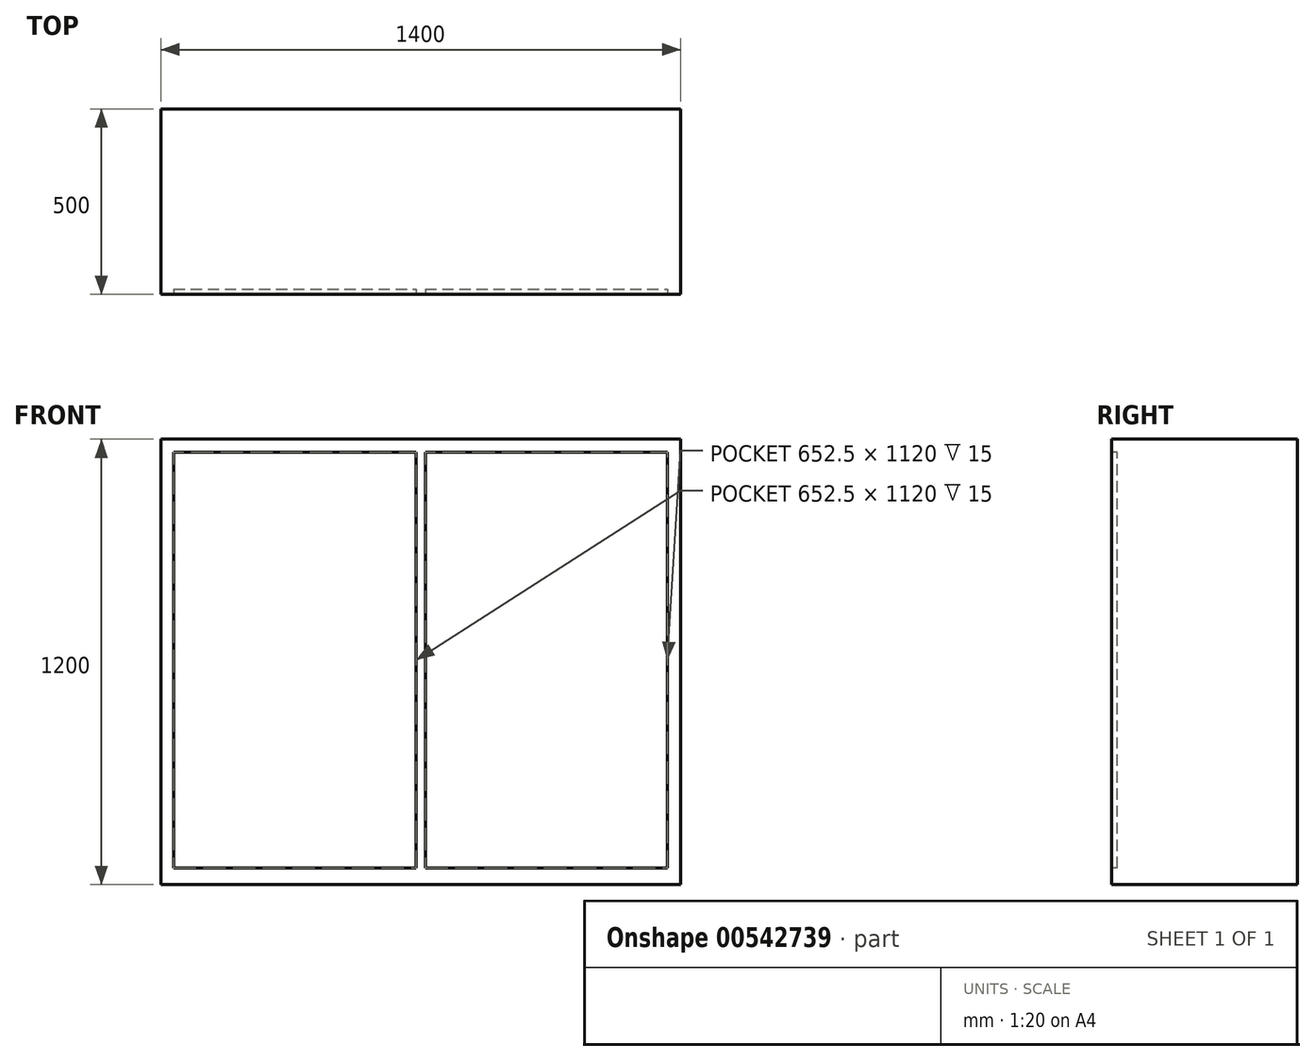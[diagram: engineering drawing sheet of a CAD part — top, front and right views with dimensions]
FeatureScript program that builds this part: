
annotation { "Feature Type Name" : "Feature", "Feature Type Description" : "" }
export const myFeature = defineFeature(function(context is Context, id is Id, definition is map)
    precondition{}
    {
        {
            var Q0;
            Q0=qCreatedBy(makeId("Top.planeOp"),FACE);
            var sketch = newSketch(context, id + "F0", { "sketchPlane" : qUnion([Q0])});
            skLineSegment(sketch, "E0.bottom", {"start": v(-700, 250) * mm, "end": v(700, 250) * mm});
            skLineSegment(sketch, "E0.top", {"start": v(-700, -250) * mm, "end": v(700, -250) * mm});
            skLineSegment(sketch, "E0.left", {"start": v(-700, 250) * mm, "end": v(-700, -250) * mm});
            skLineSegment(sketch, "E0.right", {"start": v(700, 250) * mm, "end": v(700, -250) * mm});
            skPoint(sketch, "E0.middle", {"position": v(0, 0) * mm});
            skSolve(sketch);
        }
        {
            var Q0;
            Q0 = qSketchRegion(id + "F0", true);
            extrude(context, id + "F1", {"entities" : qUnion([Q0]), "depth" : 1200 * mm, "offsetDistance" : 25 * mm});
        }
        {
            var Q0;
            Q0=makeQuery(id+"F1.opExtrude","SWEPT_FACE",FACE,{"disambiguationData":[OSD([sQuery(id+"F0.wireOp",EDGE,"E0.top")])]});
            var sketch = newSketch(context, id + "F2", { "sketchPlane" : qUnion([Q0])});
            skLineSegment(sketch, "E1.bottom", {"start": v(-665, 1165) * mm, "end": v(-12.5, 1165) * mm});
            skLineSegment(sketch, "E1.top", {"start": v(-665, 45) * mm, "end": v(-12.5, 45) * mm});
            skLineSegment(sketch, "E1.left", {"start": v(-665, 1165) * mm, "end": v(-665, 45) * mm});
            skLineSegment(sketch, "E1.right", {"start": v(-12.5, 1165) * mm, "end": v(-12.5, 45) * mm});
            skLineSegment(sketch, "E2.bottom", {"start": v(12.5, 45) * mm, "end": v(665, 45) * mm});
            skLineSegment(sketch, "E2.top", {"start": v(12.5, 1165) * mm, "end": v(665, 1165) * mm});
            skLineSegment(sketch, "E2.left", {"start": v(12.5, 45) * mm, "end": v(12.5, 1165) * mm});
            skLineSegment(sketch, "E2.right", {"start": v(665, 45) * mm, "end": v(665, 1165) * mm});
            skLineSegment(sketch, "E3", {"start": v(665, 1165) * mm, "end": v(700, 1165) * mm, "construction": true});
            skLineSegment(sketch, "E4", {"start": v(-665, 1165) * mm, "end": v(-700, 1165) * mm, "construction": true});
            skSolve(sketch);
        }
        {
            var Q0;
            Q0 = qSketchRegion(id + "F2", true);
            extrude(context, id + "F3", {"entities" : qUnion([Q0]), "operationType" : NewBodyOperationType.REMOVE, "oppositeDirection" : true, "depth" : 15 * mm, "offsetDistance" : 25 * mm});
        }
    });
